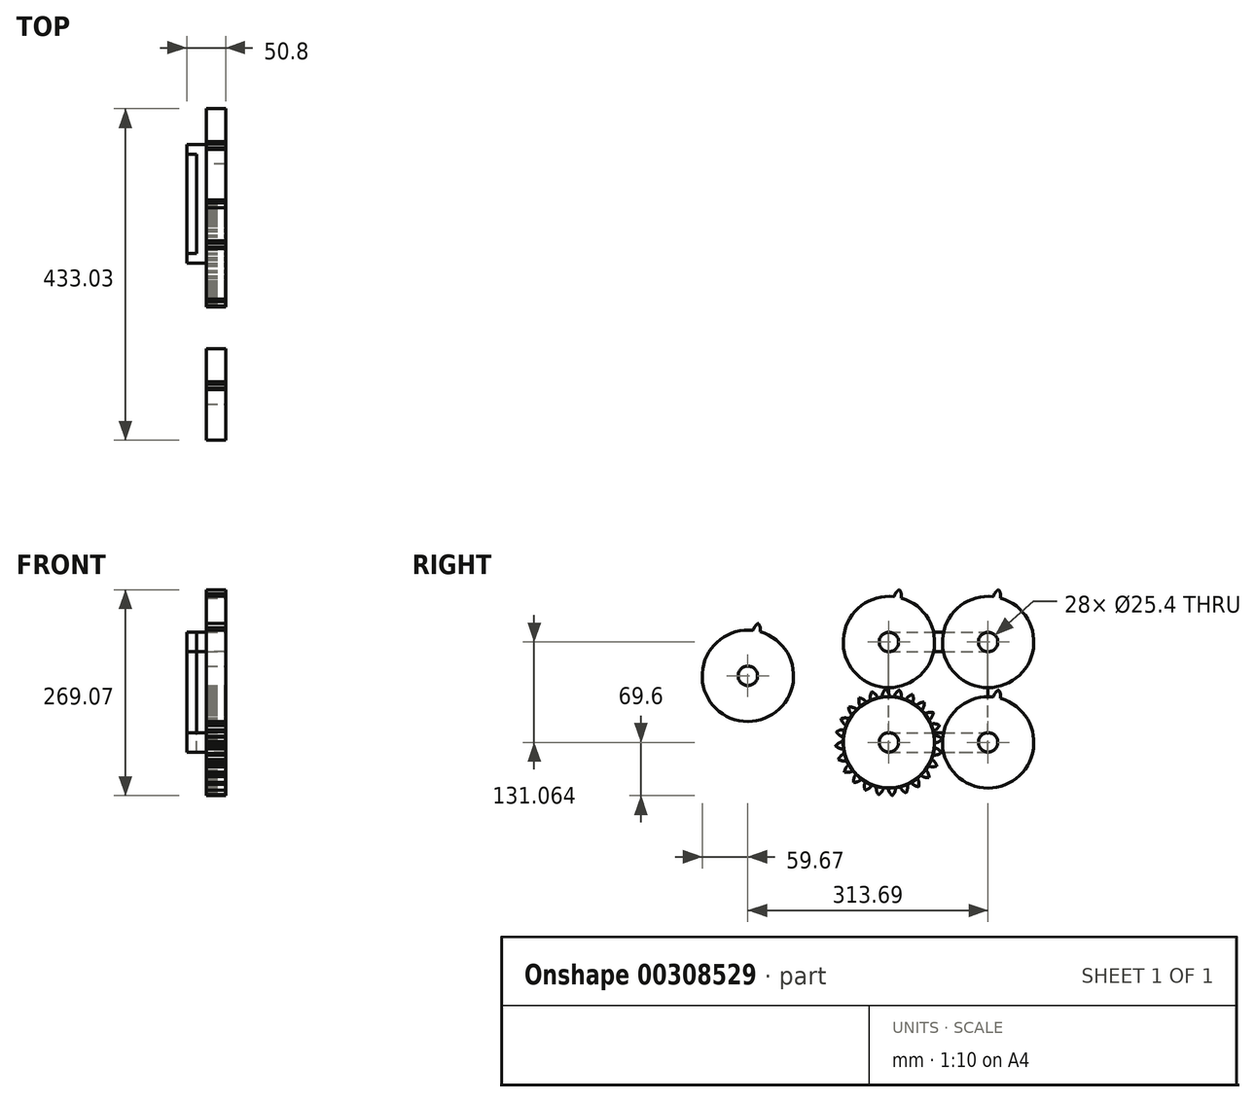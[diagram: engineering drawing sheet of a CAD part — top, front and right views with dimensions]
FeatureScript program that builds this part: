
annotation { "Feature Type Name" : "Feature", "Feature Type Description" : "" }
export const myFeature = defineFeature(function(context is Context, id is Id, definition is map)
    precondition{}
    {
        {
            var Q0;
            Q0=qCreatedBy(makeId("Right.planeOp"),FACE);
            var sketch = newSketch(context, id + "F0", { "sketchPlane" : qUnion([Q0])});
            skLineSegment(sketch, "E0.bottom", {"start": v(0, 0) * mm, "end": v(129.54, 0) * mm});
            skLineSegment(sketch, "E0.top", {"start": v(0, 25.4) * mm, "end": v(129.54, 25.4) * mm});
            skLineSegment(sketch, "E0.left", {"start": v(0, 0) * mm, "end": v(0, 25.4) * mm});
            skLineSegment(sketch, "E0.right", {"start": v(129.54, 0) * mm, "end": v(129.54, 25.4) * mm});
            skCircle(sketch, "E1", {"center": v(0, 12.7) * mm, "radius": 12.7 * mm});
            skCircle(sketch, "E2", {"center": v(129.54, 12.7) * mm, "radius": 12.7 * mm});
            skSolve(sketch);
        }
        {
            var Q0;
            {var subQ0=sQuery(id+"F0.wireOp",EDGE,"E0.left");Q0=makeQuery(id+"F0.imprint","IMPRINT",FACE,{"disambiguationData":[TD([[makeQuery(id+"F0.imprint","IMPRINT",EDGE,{"derivedFrom":subQ0}),1.0]])]});}
            var Q1;
            {var subQ0=sQuery(id+"F0.wireOp",EDGE,"E0.right");Q1=makeQuery(id+"F0.imprint","IMPRINT",FACE,{"disambiguationData":[TD([[makeQuery(id+"F0.imprint","IMPRINT",EDGE,{"derivedFrom":subQ0}),-1.0]])]});}
            var Q2;
            {var subQ0=sQuery(id+"F0.wireOp",EDGE,"E0.bottom");Q2=makeQuery(id+"F0.imprint","IMPRINT",FACE,{"disambiguationData":[TD([[makeQuery(id+"F0.imprint","IMPRINT",EDGE,{"derivedFrom":subQ0}),1.0]])]});}
            var Q3;
            {var subQ0=sQuery(id+"F0.wireOp",EDGE,"E0.left");Q3=makeQuery(id+"F0.imprint","IMPRINT",FACE,{"disambiguationData":[TD([[makeQuery(id+"F0.imprint","IMPRINT",EDGE,{"derivedFrom":subQ0}),-1.0]])]});}
            var Q4;
            {var subQ0=sQuery(id+"F0.wireOp",EDGE,"E0.right");Q4=makeQuery(id+"F0.imprint","IMPRINT",FACE,{"disambiguationData":[TD([[makeQuery(id+"F0.imprint","IMPRINT",EDGE,{"derivedFrom":subQ0}),1.0]])]});}
            extrude(context, id + "F1", {"entities" : qUnion([Q0, Q1, Q2, Q3, Q4]), "depth" : 25.4 * mm});
        }
        {
            var Q0;
            {var subQ0=sQuery(id+"F0.wireOp",EDGE,"E0.left");Q0=makeQuery(id+"F0.imprint","IMPRINT",FACE,{"disambiguationData":[TD([[makeQuery(id+"F0.imprint","IMPRINT",EDGE,{"derivedFrom":subQ0}),-1.0]])]});}
            var Q1;
            {var subQ0=sQuery(id+"F0.wireOp",EDGE,"E0.left");Q1=makeQuery(id+"F0.imprint","IMPRINT",FACE,{"disambiguationData":[TD([[makeQuery(id+"F0.imprint","IMPRINT",EDGE,{"derivedFrom":subQ0}),1.0]])]});}
            var Q2;
            {var subQ0=sQuery(id+"F0.wireOp",EDGE,"E0.right");Q2=makeQuery(id+"F0.imprint","IMPRINT",FACE,{"disambiguationData":[TD([[makeQuery(id+"F0.imprint","IMPRINT",EDGE,{"derivedFrom":subQ0}),-1.0]])]});}
            var Q3;
            {var subQ0=sQuery(id+"F0.wireOp",EDGE,"E0.right");Q3=makeQuery(id+"F0.imprint","IMPRINT",FACE,{"disambiguationData":[TD([[makeQuery(id+"F0.imprint","IMPRINT",EDGE,{"derivedFrom":subQ0}),1.0]])]});}
            extrude(context, id + "F2", {"entities" : qUnion([Q0, Q1, Q2, Q3]), "operationType" : NewBodyOperationType.ADD, "depth" : 50.8 * mm});
        }
        {
            var Q0;
            Q0=makeQuery(id+"F2.opExtrude","CAP_FACE",FACE,{"disambiguationData":[OSD([sQuery(id+"F0.wireOp",EDGE,"E1")])],"isStart":false});
            var sketch = newSketch(context, id + "F3", { "sketchPlane" : qUnion([Q0])});
            skCircle(sketch, "E3", {"center": v(0, 12.7) * mm, "radius": 12.7 * mm});
            skCircle(sketch, "E4", {"center": v(0, 12.7) * mm, "radius": 53.72 * mm, "construction": true});
            skCircle(sketch, "E5", {"center": v(0, 12.7) * mm, "radius": 58.67 * mm, "construction": true});
            skCircle(sketch, "E6", {"center": v(0, 12.7) * mm, "radius": 63.5 * mm, "construction": true});
            skLineSegment(sketch, "E7", {"start": v(0, 12.7) * mm, "end": v(0, 107.32) * mm, "construction": true});
            skLineSegment(sketch, "E8", {"start": v(0, 12.7) * mm, "end": v(-6.2, 107.26) * mm, "construction": true});
            skLineSegment(sketch, "E9", {"start": v(0, 76.2) * mm, "end": v(-72.14, 76.2) * mm, "construction": true});
            skLineSegment(sketch, "E10", {"start": v(0, 76.2) * mm, "end": v(-67.95, 51.47) * mm, "construction": true});
            skCircle(sketch, "E11", {"center": v(0, 12.7) * mm, "radius": 59.67 * mm});
            skCircle(sketch, "E12", {"center": v(0, 76.2) * mm, "radius": 14.6 * mm, "construction": true});
            skCircle(sketch, "E13", {"center": v(-13.57, 70.8) * mm, "radius": 14.6 * mm, "construction": true});
            skArc(sketch, "E14", {"start": v(0, 76.2) * mm, "mid": v(-1.9, 79.54) * mm, "end": v(-4.56, 82.3) * mm});
            skArc(sketch, "E15", {"start": v(0.95, 72.36) * mm, "mid": v(0.6, 74.31) * mm, "end": v(0, 76.2) * mm});
            skArc(sketch, "E16.MirrorCS", {"start": v(-8.29, 75.66) * mm, "mid": v(-6.85, 79.22) * mm, "end": v(-4.56, 82.3) * mm});
            skArc(sketch, "E17.MirrorCS", {"start": v(-8.73, 71.73) * mm, "mid": v(-8.63, 73.7) * mm, "end": v(-8.29, 75.66) * mm});
            skSolve(sketch);
        }
        {
            var Q0;
            Q0 = qSketchRegion(id + "F3", true);
            extrude(context, id + "F4", {"entities" : qUnion([Q0]), "oppositeDirection" : true, "depth" : 25.4 * mm});
        }
        {
            var Q0;
            Q0=makeQuery(id+"F4.opExtrude","SWEPT_BODY",BODY,{"disambiguationData":[OSD([sQuery(id+"F3.wireOp",EDGE,"E3"),sQuery(id+"F3.wireOp",EDGE,"E11"),sQuery(id+"F3.wireOp",EDGE,"E14"),sQuery(id+"F3.wireOp",EDGE,"E15"),sQuery(id+"F3.wireOp",EDGE,"E16.MirrorCS"),sQuery(id+"F3.wireOp",EDGE,"E17.MirrorCS")])]});
            var Q1;
            Q1=makeQuery(id+"F4.opExtrude","SWEPT_FACE",FACE,{"disambiguationData":[OSD([sQuery(id+"F3.wireOp",EDGE,"E11")])]});
            circularPattern(context, id + "F5", {"entities" : qUnion([Q0]), "axis" : qUnion([Q1]), "angle" : 15 * degree, "instanceCount" : 24});
        }
        {
            var Q0;
            Q0=makeQuery(id+"F5.opPattern","COPY",BODY,{"derivedFrom":makeQuery(id+"F4.opExtrude","SWEPT_BODY",BODY,{"disambiguationData":[OSD([sQuery(id+"F3.wireOp",EDGE,"E3"),sQuery(id+"F3.wireOp",EDGE,"E11"),sQuery(id+"F3.wireOp",EDGE,"E14"),sQuery(id+"F3.wireOp",EDGE,"E15"),sQuery(id+"F3.wireOp",EDGE,"E16.MirrorCS"),sQuery(id+"F3.wireOp",EDGE,"E17.MirrorCS")])]}),"instanceName":"23"});
            transform(context, id + "F6", {"entities" : qUnion([Q0]), "transformType" : TransformType.TRANSLATION_3D, "dx" : 0 * mm, "dy" : 129.54 * mm, "dz" : 0 * mm, "makeCopy" : true});
        }
        {
            var Q0;
            Q0=makeQuery(id+"F1.opExtrude","SWEPT_BODY",BODY,{"disambiguationData":[OSD([sQuery(id+"F0.wireOp",EDGE,"E0.bottom"),sQuery(id+"F0.wireOp",EDGE,"E0.top"),sQuery(id+"F0.wireOp",EDGE,"E1"),sQuery(id+"F0.wireOp",EDGE,"E2")])]});
            transform(context, id + "F7", {"entities" : qUnion([Q0]), "transformType" : TransformType.TRANSLATION_3D, "dx" : 0 * mm, "dy" : 0 * mm, "dz" : 131.06 * mm, "makeCopy" : true});
        }
        {
            var Q0;
            Q0=makeQuery(id+"F5.opPattern","COPY",BODY,{"derivedFrom":makeQuery(id+"F4.opExtrude","SWEPT_BODY",BODY,{"disambiguationData":[OSD([sQuery(id+"F3.wireOp",EDGE,"E3"),sQuery(id+"F3.wireOp",EDGE,"E11"),sQuery(id+"F3.wireOp",EDGE,"E14"),sQuery(id+"F3.wireOp",EDGE,"E15"),sQuery(id+"F3.wireOp",EDGE,"E16.MirrorCS"),sQuery(id+"F3.wireOp",EDGE,"E17.MirrorCS")])]}),"instanceName":"23"});
            transform(context, id + "F8", {"entities" : qUnion([Q0]), "transformType" : TransformType.TRANSLATION_3D, "dx" : 0 * mm, "dy" : 0 * mm, "dz" : 131.06 * mm, "makeCopy" : true});
        }
        {
            var Q0;
            Q0=makeQuery(id+"F6.opPattern","COPY",BODY,{"derivedFrom":makeQuery(id+"F5.opPattern","COPY",BODY,{"derivedFrom":makeQuery(id+"F4.opExtrude","SWEPT_BODY",BODY,{"disambiguationData":[OSD([sQuery(id+"F3.wireOp",EDGE,"E3"),sQuery(id+"F3.wireOp",EDGE,"E11"),sQuery(id+"F3.wireOp",EDGE,"E14"),sQuery(id+"F3.wireOp",EDGE,"E15"),sQuery(id+"F3.wireOp",EDGE,"E16.MirrorCS"),sQuery(id+"F3.wireOp",EDGE,"E17.MirrorCS")])]}),"instanceName":"23"}),"instanceName":"1"});
            transform(context, id + "F9", {"entities" : qUnion([Q0]), "transformType" : TransformType.TRANSLATION_3D, "dx" : 0 * mm, "dy" : 0 * mm, "dz" : 131.06 * mm, "makeCopy" : true});
        }
        {
            var Q0;
            Q0=makeQuery(id+"F7.opPattern","COPY",FACE,{"derivedFrom":makeQuery(id+"F1.opExtrude","CAP_FACE",FACE,{"disambiguationData":[OSD([sQuery(id+"F0.wireOp",EDGE,"E0.bottom"),sQuery(id+"F0.wireOp",EDGE,"E0.top"),sQuery(id+"F0.wireOp",EDGE,"E1"),sQuery(id+"F0.wireOp",EDGE,"E2")])],"isStart":true}),"instanceName":"1"});
            var sketch = newSketch(context, id + "F10", { "sketchPlane" : qUnion([Q0])});
            skLineSegment(sketch, "E18.bottom", {"start": v(0, -0.5) * mm, "end": v(-129.54, -0.5) * mm});
            skLineSegment(sketch, "E18.top", {"start": v(0, 156.46) * mm, "end": v(-129.54, 156.46) * mm});
            skLineSegment(sketch, "E18.left", {"start": v(0, -0.5) * mm, "end": v(0, 156.46) * mm});
            skLineSegment(sketch, "E18.right", {"start": v(-129.54, -0.5) * mm, "end": v(-129.54, 156.46) * mm});
            skSolve(sketch);
        }
        {
            var Q0;
            {var subQ0=sQuery(id+"F10.wireOp",EDGE,"E18.bottom");Q0=makeQuery(id+"F10.imprint","IMPRINT",FACE,{"disambiguationData":[TD([[makeQuery(id+"F10.imprint","IMPRINT",EDGE,{"derivedFrom":subQ0}),-1.0]])]});}
            var Q1;
            {var subQ0=sQuery(id+"F10.wireOp",EDGE,"E18.top");Q1=makeQuery(id+"F10.imprint","IMPRINT",FACE,{"disambiguationData":[TD([[makeQuery(id+"F10.imprint","IMPRINT",EDGE,{"derivedFrom":subQ0}),1.0]])]});}
            extrude(context, id + "F11", {"entities" : qUnion([Q0, Q1]), "oppositeDirection" : true, "depth" : 12.7 * mm});
        }
        {
            var Q0;
            Q0=makeQuery(id+"F5.opPattern","COPY",BODY,{"derivedFrom":makeQuery(id+"F4.opExtrude","SWEPT_BODY",BODY,{"disambiguationData":[OSD([sQuery(id+"F3.wireOp",EDGE,"E3"),sQuery(id+"F3.wireOp",EDGE,"E11"),sQuery(id+"F3.wireOp",EDGE,"E14"),sQuery(id+"F3.wireOp",EDGE,"E15"),sQuery(id+"F3.wireOp",EDGE,"E16.MirrorCS"),sQuery(id+"F3.wireOp",EDGE,"E17.MirrorCS")])]}),"instanceName":"23"});
            transform(context, id + "F12", {"entities" : qUnion([Q0]), "transformType" : TransformType.TRANSLATION_3D, "dx" : 0 * mm, "dy" : -184.15 * mm, "dz" : 86.87 * mm, "makeCopy" : true});
        }
    });
